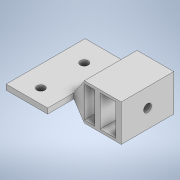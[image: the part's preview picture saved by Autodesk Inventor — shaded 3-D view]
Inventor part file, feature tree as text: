
AUTODESK INVENTOR PART (.ipt)
format: ipt  version: 2020 (Build 240168000, 168)  size: 189,952 bytes
history: native  units: in
note: dims shown in document units (in); Inventor stores cm internally (conversion verified against a paired STEP export)
features: extrude x7, sketch x7
ambient origin geometry x8: Origin, YZ Plane, XZ Plane, XY Plane, X Axis, Y Axis, Z Axis, Center Point
bodies: Solid1 (feature_tree)
feature tree (14):
  extrude  "Extrusion1"  Depth=1.0in
  extrude  "Extrusion2"  Depth=0.2in TaperAngle=0.0deg
  extrude  "Extrusion3"  Depth=0.1in
  extrude  "Extrusion5"  Depth=0.6in
  extrude  "Extrusion6"  Depth=0.6in
  extrude  "Extrusion7"  Depth=0.5625in TaperAngle=0.0deg
  extrude  "Extrusion8"  Depth=0.7in
  sketch  "Sketch1"  dims[d0=0.7874in d1=1.0in]
  sketch  "Sketch2"  dims[d2=0.1in d3=0.0in d4=0.2in d5=0.0in]
  sketch  "Sketch4"  dims[d6=0.3in d7=0.1in]
  sketch  "Sketch6"  dims[d9=0.3in d10=0.6in]
  sketch  "Sketch7"  dims[d11=1.0in d12=0.0in d16=0.6in]
  sketch  "Sketch8"  dims[d17=0.15in d18=0.5625in d19=0.0in]
  sketch  "Sketch9"  dims[d20=0.5906in d21=0.15in d22=1.125in d23=0.0in d24=0.5in d25=0.0in d26=0.15in d27=3.0in d28=0.0in d30=0.7in]
